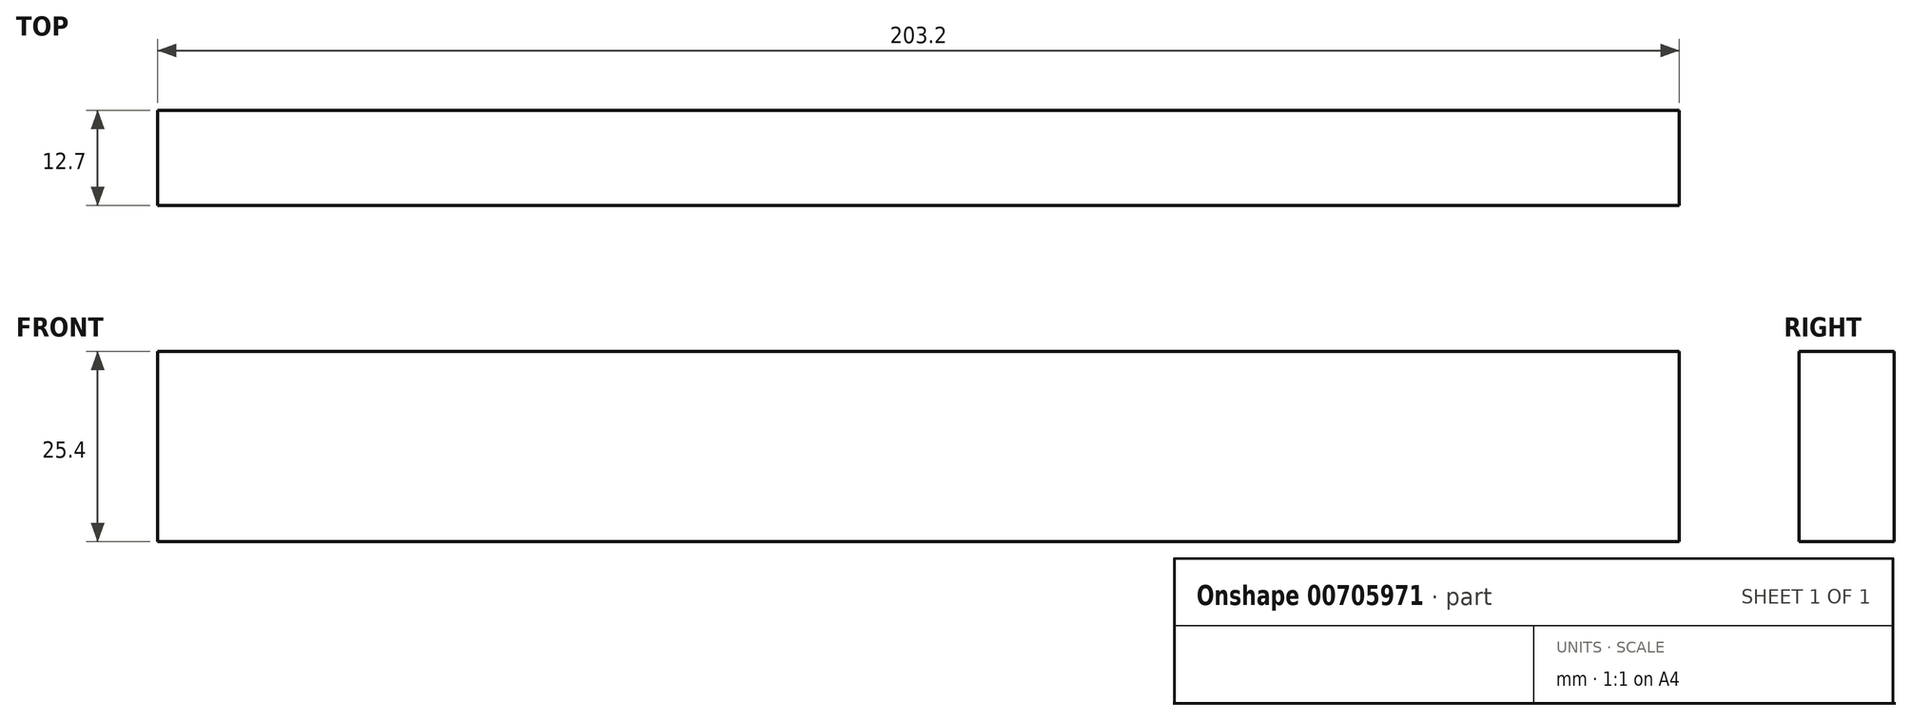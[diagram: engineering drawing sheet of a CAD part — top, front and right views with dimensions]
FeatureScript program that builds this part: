
annotation { "Feature Type Name" : "Feature", "Feature Type Description" : "" }
export const myFeature = defineFeature(function(context is Context, id is Id, definition is map)
    precondition{}
    {
        {
            var Q0;
            Q0=qCreatedBy(makeId("Top.planeOp"),FACE);
            var sketch = newSketch(context, id + "F0", { "sketchPlane" : qUnion([Q0])});
            skLineSegment(sketch, "E0.bottom", {"start": v(-48.92, 62.7) * mm, "end": v(154.28, 62.7) * mm});
            skLineSegment(sketch, "E0.top", {"start": v(-48.92, 50) * mm, "end": v(154.28, 50) * mm});
            skLineSegment(sketch, "E0.left", {"start": v(-48.92, 62.7) * mm, "end": v(-48.92, 50) * mm});
            skLineSegment(sketch, "E0.right", {"start": v(154.28, 62.7) * mm, "end": v(154.28, 50) * mm});
            skSolve(sketch);
        }
        {
            var Q0;
            Q0 = qSketchRegion(id + "F0", true);
            extrude(context, id + "F1", {"entities" : qUnion([Q0]), "depth" : 25.4 * mm, "offsetDistance" : 25.4 * mm});
        }
    });
